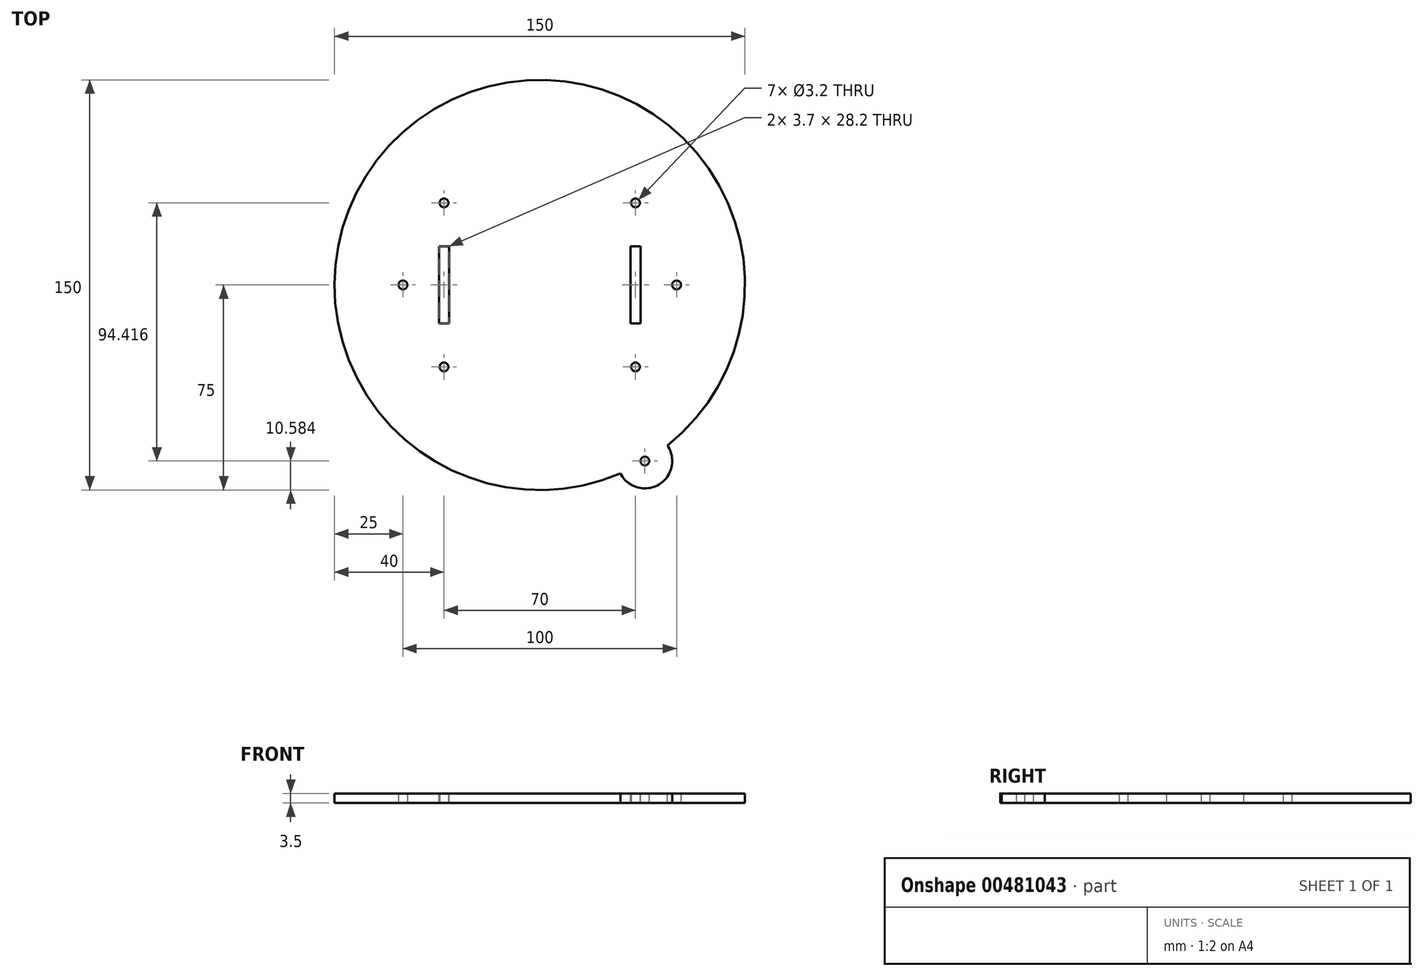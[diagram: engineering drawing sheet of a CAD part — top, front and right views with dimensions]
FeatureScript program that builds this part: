
annotation { "Feature Type Name" : "Feature", "Feature Type Description" : "" }
export const myFeature = defineFeature(function(context is Context, id is Id, definition is map)
    precondition{}
    {
        {
            var Q0;
            Q0=qCreatedBy(makeId("Top.planeOp"),FACE);
            var sketch = newSketch(context, id + "F0", { "sketchPlane" : qUnion([Q0])});
            skLineSegment(sketch, "E0", {"start": v(0, 0) * mm, "end": v(75, 0) * mm});
            skCircle(sketch, "E1", {"center": v(0, 0) * mm, "radius": 75 * mm});
            skSolve(sketch);
        }
        {
            var Q0;
            Q0 = qSketchRegion(id + "F0", true);
            extrude(context, id + "F1", {"entities" : qUnion([Q0]), "depth" : 3.5 * mm});
        }
        {
            var Q0;
            Q0=qCreatedBy(makeId("Top.planeOp"),FACE);
            var sketch = newSketch(context, id + "F2", { "sketchPlane" : qUnion([Q0])});
            skLineSegment(sketch, "E2.bottom", {"start": v(35, -30) * mm, "end": v(-35, -30) * mm});
            skLineSegment(sketch, "E2.top", {"start": v(35, 30) * mm, "end": v(-35, 30) * mm});
            skLineSegment(sketch, "E2.left", {"start": v(35, -30) * mm, "end": v(35, 30) * mm});
            skLineSegment(sketch, "E2.right", {"start": v(-35, -30) * mm, "end": v(-35, 30) * mm});
            skPoint(sketch, "E2.middle", {"position": v(0, 0) * mm});
            skLineSegment(sketch, "E3", {"start": v(-50, 0) * mm, "end": v(50, 0) * mm});
            skLineSegment(sketch, "E4", {"start": v(-20, 0) * mm, "end": v(20, 0) * mm});
            skCircle(sketch, "E5", {"center": v(-20, 0) * mm, "radius": 1.6 * mm});
            skCircle(sketch, "E6", {"center": v(-35, 30) * mm, "radius": 1.6 * mm});
            skCircle(sketch, "E7", {"center": v(-50, 0) * mm, "radius": 1.6 * mm});
            skCircle(sketch, "E8", {"center": v(-35, -30) * mm, "radius": 1.6 * mm});
            skCircle(sketch, "E9", {"center": v(0, 0) * mm, "radius": 2.6 * mm});
            skCircle(sketch, "E10", {"center": v(35, 30) * mm, "radius": 1.6 * mm});
            skCircle(sketch, "E11", {"center": v(50, 0) * mm, "radius": 1.6 * mm});
            skCircle(sketch, "E12", {"center": v(20, 0) * mm, "radius": 1.6 * mm});
            skCircle(sketch, "E13", {"center": v(35, -30) * mm, "radius": 1.6 * mm});
            skSolve(sketch);
        }
        {
            var Q0;
            Q0=makeQuery(id+"F2.imprint","IMPRINT",FACE,{"disambiguationData":[TD([[makeQuery(id+"F2.imprint","IMPRINT",EDGE,{"derivedFrom":sQuery(id+"F2.wireOp",EDGE,"E7")}),1.0]])]});
            var Q1;
            Q1=makeQuery(id+"F2.imprint","IMPRINT",FACE,{"disambiguationData":[TD([[makeQuery(id+"F2.imprint","IMPRINT",EDGE,{"derivedFrom":sQuery(id+"F2.wireOp",EDGE,"E11")}),1.0]])]});
            var Q2;
            {var subQ0=sQuery(id+"F2.wireOp",EDGE,"E2.left");var subQ1=sQuery(id+"F2.wireOp",EDGE,"E2.bottom");var subQ2=makeQuery(id+"F2.imprint","INTERSECT",VERTEX,{"derivedFrom":[subQ1,subQ0]});Q2=makeQuery(id+"F2.imprint","IMPRINT",FACE,{"disambiguationData":[TD([[makeQuery(id+"F2.imprint","IMPRINT",EDGE,{"disambiguationData":[TD([[subQ2,-1.0]])],"derivedFrom":subQ1}),1.0]])]});}
            var Q3;
            {var subQ0=sQuery(id+"F2.wireOp",EDGE,"E2.right");var subQ1=sQuery(id+"F2.wireOp",EDGE,"E2.bottom");var subQ2=makeQuery(id+"F2.imprint","INTERSECT",VERTEX,{"derivedFrom":[subQ1,subQ0]});Q3=makeQuery(id+"F2.imprint","IMPRINT",FACE,{"disambiguationData":[TD([[makeQuery(id+"F2.imprint","IMPRINT",EDGE,{"disambiguationData":[TD([[subQ2,1.0]])],"derivedFrom":subQ1}),1.0]])]});}
            var Q4;
            {var subQ0=sQuery(id+"F2.wireOp",EDGE,"E2.left");var subQ1=sQuery(id+"F2.wireOp",EDGE,"E2.top");var subQ2=makeQuery(id+"F2.imprint","INTERSECT",VERTEX,{"derivedFrom":[subQ1,subQ0]});Q4=makeQuery(id+"F2.imprint","IMPRINT",FACE,{"disambiguationData":[TD([[makeQuery(id+"F2.imprint","IMPRINT",EDGE,{"disambiguationData":[TD([[subQ2,-1.0]])],"derivedFrom":subQ1}),-1.0]])]});}
            var Q5;
            {var subQ0=sQuery(id+"F2.wireOp",EDGE,"E2.right");var subQ1=sQuery(id+"F2.wireOp",EDGE,"E2.top");var subQ2=makeQuery(id+"F2.imprint","INTERSECT",VERTEX,{"derivedFrom":[subQ1,subQ0]});Q5=makeQuery(id+"F2.imprint","IMPRINT",FACE,{"disambiguationData":[TD([[makeQuery(id+"F2.imprint","IMPRINT",EDGE,{"disambiguationData":[TD([[subQ2,1.0]])],"derivedFrom":subQ1}),-1.0]])]});}
            var Q6;
            {var subQ0=sQuery(id+"F2.wireOp",EDGE,"E2.left");var subQ1=sQuery(id+"F2.wireOp",EDGE,"E2.bottom");var subQ2=makeQuery(id+"F2.imprint","INTERSECT",VERTEX,{"derivedFrom":[subQ1,subQ0]});Q6=makeQuery(id+"F2.imprint","IMPRINT",FACE,{"disambiguationData":[TD([[makeQuery(id+"F2.imprint","IMPRINT",EDGE,{"disambiguationData":[TD([[subQ2,-1.0]])],"derivedFrom":subQ1}),-1.0]])]});}
            var Q7;
            {var subQ0=sQuery(id+"F2.wireOp",EDGE,"E2.right");var subQ1=sQuery(id+"F2.wireOp",EDGE,"E2.bottom");var subQ2=makeQuery(id+"F2.imprint","INTERSECT",VERTEX,{"derivedFrom":[subQ1,subQ0]});Q7=makeQuery(id+"F2.imprint","IMPRINT",FACE,{"disambiguationData":[TD([[makeQuery(id+"F2.imprint","IMPRINT",EDGE,{"disambiguationData":[TD([[subQ2,1.0]])],"derivedFrom":subQ1}),-1.0]])]});}
            var Q8;
            {var subQ0=sQuery(id+"F2.wireOp",EDGE,"E2.left");var subQ1=sQuery(id+"F2.wireOp",EDGE,"E2.top");var subQ2=makeQuery(id+"F2.imprint","INTERSECT",VERTEX,{"derivedFrom":[subQ1,subQ0]});Q8=makeQuery(id+"F2.imprint","IMPRINT",FACE,{"disambiguationData":[TD([[makeQuery(id+"F2.imprint","IMPRINT",EDGE,{"disambiguationData":[TD([[subQ2,-1.0]])],"derivedFrom":subQ1}),1.0]])]});}
            var Q9;
            {var subQ0=sQuery(id+"F2.wireOp",EDGE,"E2.right");var subQ1=sQuery(id+"F2.wireOp",EDGE,"E2.top");var subQ2=makeQuery(id+"F2.imprint","INTERSECT",VERTEX,{"derivedFrom":[subQ1,subQ0]});Q9=makeQuery(id+"F2.imprint","IMPRINT",FACE,{"disambiguationData":[TD([[makeQuery(id+"F2.imprint","IMPRINT",EDGE,{"disambiguationData":[TD([[subQ2,1.0]])],"derivedFrom":subQ1}),1.0]])]});}
            var Q10;
            {var subQ0=sQuery(id+"F2.wireOp",EDGE,"E4");var subQ1=sQuery(id+"F2.wireOp",EDGE,"E3");var subQ2=makeQuery(id+"F2.imprint","INTERSECT",VERTEX,{"disambiguationData":[OD(0.0)],"derivedFrom":[subQ1,subQ0]});Q10=makeQuery(id+"F2.imprint","IMPRINT",FACE,{"disambiguationData":[TD([[makeQuery(id+"F2.imprint","IMPRINT",EDGE,{"disambiguationData":[TD([[subQ2,1.0]])],"derivedFrom":subQ1}),1.0]])]});}
            var Q11;
            {var subQ0=sQuery(id+"F2.wireOp",EDGE,"E4");var subQ1=sQuery(id+"F2.wireOp",EDGE,"E3");var subQ2=makeQuery(id+"F2.imprint","INTERSECT",VERTEX,{"disambiguationData":[OD(0.0)],"derivedFrom":[subQ1,subQ0]});Q11=makeQuery(id+"F2.imprint","IMPRINT",FACE,{"disambiguationData":[TD([[makeQuery(id+"F2.imprint","IMPRINT",EDGE,{"disambiguationData":[TD([[subQ2,1.0]])],"derivedFrom":subQ1}),-1.0]])]});}
            var Q12;
            {var subQ0=sQuery(id+"F2.wireOp",EDGE,"E4");var subQ1=sQuery(id+"F2.wireOp",EDGE,"E3");var subQ2=makeQuery(id+"F2.imprint","INTERSECT",VERTEX,{"disambiguationData":[OD(1.0)],"derivedFrom":[subQ1,subQ0]});Q12=makeQuery(id+"F2.imprint","IMPRINT",FACE,{"disambiguationData":[TD([[makeQuery(id+"F2.imprint","IMPRINT",EDGE,{"disambiguationData":[TD([[subQ2,-1.0]])],"derivedFrom":subQ1}),1.0]])]});}
            var Q13;
            {var subQ0=sQuery(id+"F2.wireOp",EDGE,"E4");var subQ1=sQuery(id+"F2.wireOp",EDGE,"E3");var subQ2=makeQuery(id+"F2.imprint","INTERSECT",VERTEX,{"disambiguationData":[OD(1.0)],"derivedFrom":[subQ1,subQ0]});Q13=makeQuery(id+"F2.imprint","IMPRINT",FACE,{"disambiguationData":[TD([[makeQuery(id+"F2.imprint","IMPRINT",EDGE,{"disambiguationData":[TD([[subQ2,-1.0]])],"derivedFrom":subQ1}),-1.0]])]});}
            var Q14;
            {var subQ0=sQuery(id+"F2.wireOp",EDGE,"E9");var subQ1=sQuery(id+"F2.wireOp",EDGE,"E4");var subQ2=makeQuery(id+"F2.imprint","INTERSECT",VERTEX,{"disambiguationData":[OD(0.0)],"derivedFrom":[subQ1,subQ0]});Q14=makeQuery(id+"F2.imprint","IMPRINT",FACE,{"disambiguationData":[TD([[makeQuery(id+"F2.imprint","IMPRINT",EDGE,{"disambiguationData":[TD([[subQ2,-1.0]])],"derivedFrom":subQ1}),-1.0]])]});}
            var Q15;
            {var subQ0=sQuery(id+"F2.wireOp",EDGE,"E9");var subQ1=sQuery(id+"F2.wireOp",EDGE,"E4");var subQ2=makeQuery(id+"F2.imprint","INTERSECT",VERTEX,{"disambiguationData":[OD(0.0)],"derivedFrom":[subQ1,subQ0]});Q15=makeQuery(id+"F2.imprint","IMPRINT",FACE,{"disambiguationData":[TD([[makeQuery(id+"F2.imprint","IMPRINT",EDGE,{"disambiguationData":[TD([[subQ2,-1.0]])],"derivedFrom":subQ1}),1.0]])]});}
            extrude(context, id + "F3", {"entities" : qUnion([Q0, Q1, Q2, Q3, Q4, Q5, Q6, Q7, Q8, Q9, Q10, Q11, Q12, Q13, Q14, Q15]), "operationType" : NewBodyOperationType.REMOVE, "depth" : 3.5 * mm});
        }
        {
            var Q0;
            Q0=makeQuery(id+"F1.opExtrude","CAP_FACE",FACE,{"disambiguationData":[OSD([sQuery(id+"F0.wireOp",EDGE,"E1")])],"isStart":false});
            var sketch = newSketch(context, id + "F4", { "sketchPlane" : qUnion([Q0])});
            skCircle(sketch, "E14", {"center": v(38.41, -64.42) * mm, "radius": 10 * mm});
            skSolve(sketch);
        }
        {
            var Q0;
            {var subQ0=sQuery(id+"F4.wireOp",EDGE,"E14");var subQ1=makeQuery(id+"F1.opExtrude","CAP_EDGE",EDGE,{"disambiguationData":[OSD([sQuery(id+"F0.wireOp",EDGE,"E1")])],"isStart":false});var subQ2=makeQuery(id+"F4.imprint","INTERSECT",VERTEX,{"disambiguationData":[OD(0.0)],"derivedFrom":[subQ1,subQ0]});Q0=makeQuery(id+"F4.imprint","IMPRINT",FACE,{"disambiguationData":[TD([[makeQuery(id+"F4.imprint","IMPRINT",EDGE,{"disambiguationData":[TD([[subQ2,-1.0]])],"derivedFrom":subQ0}),1.0]])]});}
            extrude(context, id + "F5", {"entities" : qUnion([Q0]), "operationType" : NewBodyOperationType.ADD, "depth" : -3.5 * mm, "offsetDistance" : 25 * mm});
        }
        {
            var Q0;
            {var subQ0=sQuery(id+"F0.wireOp",EDGE,"E1");Q0=makeQuery(id+"F5.boolean.opBoolean","MERGE",FACE,{"derivedFrom":[makeQuery(id+"F1.opExtrude","CAP_FACE",FACE,{"disambiguationData":[OSD([subQ0])],"isStart":false}),makeQuery(id+"F5.opExtrude","CAP_FACE",FACE,{"disambiguationData":[OSD([subQ0,sQuery(id+"F4.wireOp",EDGE,"9CzIgjQf-mTWB-3Cu6-MCBA-TOyM93C9ZrCN")])],"isStart":true})]});}
            var sketch = newSketch(context, id + "F6", { "sketchPlane" : qUnion([Q0])});
            skCircle(sketch, "E15", {"center": v(38.41, -64.42) * mm, "radius": 1.6 * mm});
            skSolve(sketch);
        }
        {
            var Q0;
            Q0 = qSketchRegion(id + "F6", true);
            extrude(context, id + "F7", {"entities" : qUnion([Q0]), "operationType" : NewBodyOperationType.REMOVE, "oppositeDirection" : true, "depth" : 3.5 * mm, "offsetDistance" : 25 * mm});
        }
        {
            var Q0;
            Q0=makeQuery(id+"F5.boolean.opBoolean","MERGE",FACE,{"derivedFrom":[makeQuery(id+"F1.opExtrude","CAP_FACE",FACE,{"disambiguationData":[OSD([sQuery(id+"F0.wireOp",EDGE,"E1")])],"isStart":false}),makeQuery(id+"F5.opExtrude","CAP_FACE",FACE,{"disambiguationData":[OSD([sQuery(id+"F4.wireOp",EDGE,"Jrb6qGLP-msVS-cme0-7Mwg-QJaZIJd2HZM8")])],"isStart":true})]});
            var sketch = newSketch(context, id + "F8", { "sketchPlane" : qUnion([Q0])});
            skLineSegment(sketch, "E16", {"start": v(-35, 30) * mm, "end": v(-35, -30) * mm});
            skLineSegment(sketch, "E17.bottom", {"start": v(-33.15, -14.1) * mm, "end": v(-36.85, -14.1) * mm});
            skLineSegment(sketch, "E17.top", {"start": v(-33.15, 14.1) * mm, "end": v(-36.85, 14.1) * mm});
            skLineSegment(sketch, "E17.left", {"start": v(-33.15, -14.1) * mm, "end": v(-33.15, 14.1) * mm});
            skLineSegment(sketch, "E17.right", {"start": v(-36.85, -14.1) * mm, "end": v(-36.85, 14.1) * mm});
            skPoint(sketch, "E17.middle", {"position": v(-35, 0) * mm});
            skLineSegment(sketch, "E18", {"start": v(35, 30) * mm, "end": v(35, -30) * mm});
            skLineSegment(sketch, "E19.bottom", {"start": v(36.85, -14.1) * mm, "end": v(33.15, -14.1) * mm});
            skLineSegment(sketch, "E19.top", {"start": v(36.85, 14.1) * mm, "end": v(33.15, 14.1) * mm});
            skLineSegment(sketch, "E19.left", {"start": v(36.85, -14.1) * mm, "end": v(36.85, 14.1) * mm});
            skLineSegment(sketch, "E19.right", {"start": v(33.15, -14.1) * mm, "end": v(33.15, 14.1) * mm});
            skPoint(sketch, "E19.middle", {"position": v(35, 0) * mm});
            skSolve(sketch);
        }
        {
            var Q0;
            Q0 = qSketchRegion(id + "F8", true);
            extrude(context, id + "F9", {"entities" : qUnion([Q0]), "operationType" : NewBodyOperationType.REMOVE, "endBound" : BoundingType.THROUGH_ALL, "oppositeDirection" : true, "depth" : 25 * mm, "offsetDistance" : 25 * mm});
        }
    });
